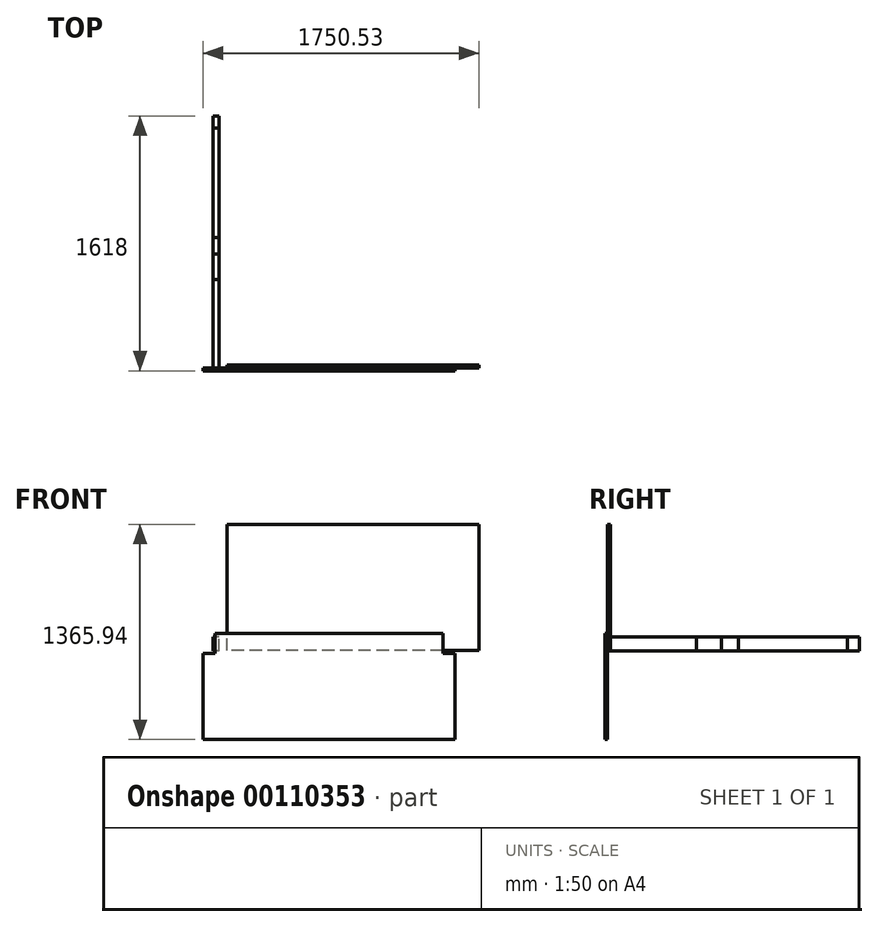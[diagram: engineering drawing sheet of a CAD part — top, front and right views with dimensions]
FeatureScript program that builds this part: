
annotation { "Feature Type Name" : "Feature", "Feature Type Description" : "" }
export const myFeature = defineFeature(function(context is Context, id is Id, definition is map)
    precondition{}
    {
        {
            assignVariable(context, id + "F0", {"name" : "WorkbenchWidth", "anyValue" : 1600});
        }
        {
            assignVariable(context, id + "F1", {"name" : "WorkbenchDepth", "anyValue" : 800});
        }
        {
            assignVariable(context, id + "F2", {"name" : "WorkbenchHeight", "anyValue" : 830});
        }
        {
            assignVariable(context, id + "F3", {"name" : "TimberWidth", "anyValue" : 89});
        }
        {
            assignVariable(context, id + "F4", {"name" : "TimberThickness", "anyValue" : 38});
        }
        {
            var Q0;
            Q0=qCreatedBy(makeId("Front.planeOp"),FACE);
            var sketch = newSketch(context, id + "F5", { "sketchPlane" : qUnion([Q0])});
            skLineSegment(sketch, "E0.bottom", {"start": v(19, -44.5) * mm, "end": v(-19, -44.5) * mm});
            skLineSegment(sketch, "E0.top", {"start": v(19, 44.5) * mm, "end": v(-19, 44.5) * mm});
            skLineSegment(sketch, "E0.left", {"start": v(19, -44.5) * mm, "end": v(19, 44.5) * mm});
            skLineSegment(sketch, "E0.right", {"start": v(-19, -44.5) * mm, "end": v(-19, 44.5) * mm});
            skPoint(sketch, "E0.middle", {"position": v(0, 0) * mm});
            skSolve(sketch);
        }
        {
            var Q0;
            Q0=makeQuery(id+"F5.imprint","IMPRINT",FACE,{"disambiguationData":[TD([[makeQuery(id+"F5.imprint","IMPRINT",EDGE,{"derivedFrom":sQuery(id+"F5.wireOp",EDGE,"E0.bottom")}),-1.0]])]});
            extrude(context, id + "F6", {"entities" : qUnion([Q0]), "oppositeDirection" : true, "depth" : (getVariable(context, 'WorkbenchWidth')) * mm});
        }
        {
            var Q0;
            Q0 = qSketchRegion(id + "F5", true);
            extrude(context, id + "F7", {"entities" : qUnion([Q0]), "oppositeDirection" : true, "depth" : (getVariable(context, 'WorkbenchDepth') - 2 * getVariable(context, 'TimberThickness')) * mm});
        }
        {
            var Q0;
            Q0 = qSketchRegion(id + "F5", true);
            extrude(context, id + "F8", {"entities" : qUnion([Q0]), "oppositeDirection" : true, "depth" : (getVariable(context, 'WorkbenchHeight')) * mm});
        }
        {
            var Q0;
            Q0 = qSketchRegion(id + "F5", true);
            extrude(context, id + "F9", {"entities" : qUnion([Q0]), "oppositeDirection" : true, "depth" : (getVariable(context, 'WorkbenchHeight') - 3 * getVariable(context, 'TimberWidth')) * mm});
        }
        {
            var Q0;
            Q0=qCreatedBy(makeId("Front.planeOp"),FACE);
            var sketch = newSketch(context, id + "F10", { "sketchPlane" : qUnion([Q0])});
            skLineSegment(sketch, "E1.bottom", {"start": v(1669.74, -41.64) * mm, "end": v(69.74, -41.64) * mm});
            skLineSegment(sketch, "E1.top", {"start": v(1669.74, 758.36) * mm, "end": v(69.74, 758.36) * mm});
            skLineSegment(sketch, "E1.left", {"start": v(1669.74, -41.64) * mm, "end": v(1669.74, 758.36) * mm});
            skLineSegment(sketch, "E1.right", {"start": v(69.74, -41.64) * mm, "end": v(69.74, 758.36) * mm});
            skPoint(sketch, "E1.middle", {"position": v(869.74, 358.36) * mm});
            skSolve(sketch);
        }
        {
            var Q0;
            Q0=makeQuery(id+"F10.imprint","IMPRINT",FACE,{"disambiguationData":[TD([[makeQuery(id+"F10.imprint","IMPRINT",EDGE,{"derivedFrom":sQuery(id+"F10.wireOp",EDGE,"E1.bottom")}),-1.0]])]});
            extrude(context, id + "F11", {"entities" : qUnion([Q0]), "oppositeDirection" : true, "depth" : 18 * mm});
        }
        {
            var Q0;
            Q0 = qSketchRegion(id + "F5", true);
            extrude(context, id + "F12", {"entities" : qUnion([Q0]), "oppositeDirection" : true, "depth" : (getVariable(context, 'WorkbenchWidth') - 2 * getVariable(context, 'TimberThickness')) * mm});
        }
        {
            var Q0;
            Q0=qCreatedBy(makeId("Front.planeOp"),FACE);
            var sketch = newSketch(context, id + "F13", { "sketchPlane" : qUnion([Q0])});
            skLineSegment(sketch, "E2", {"start": v(-4.79, 65.42) * mm, "end": v(-4.79, -61.58) * mm});
            skLineSegment(sketch, "E3", {"start": v(-4.79, -61.58) * mm, "end": v(-80.79, -61.58) * mm});
            skLineSegment(sketch, "E4", {"start": v(-80.79, -61.58) * mm, "end": v(-80.79, -607.58) * mm});
            skLineSegment(sketch, "E5", {"start": v(-80.79, -607.58) * mm, "end": v(1519.21, -607.58) * mm});
            skLineSegment(sketch, "E6", {"start": v(1519.21, -607.58) * mm, "end": v(1519.21, -61.58) * mm});
            skLineSegment(sketch, "E7", {"start": v(1519.21, -61.58) * mm, "end": v(1443.21, -61.58) * mm});
            skLineSegment(sketch, "E8", {"start": v(1443.21, -61.58) * mm, "end": v(1443.21, 65.42) * mm});
            skLineSegment(sketch, "E9", {"start": v(1443.21, 65.42) * mm, "end": v(-4.79, 65.42) * mm});
            skSolve(sketch);
        }
        {
            var Q0;
            Q0 = qSketchRegion(id + "F13", true);
            extrude(context, id + "F14", {"entities" : qUnion([Q0]), "depth" : 18 * mm});
        }
    });
